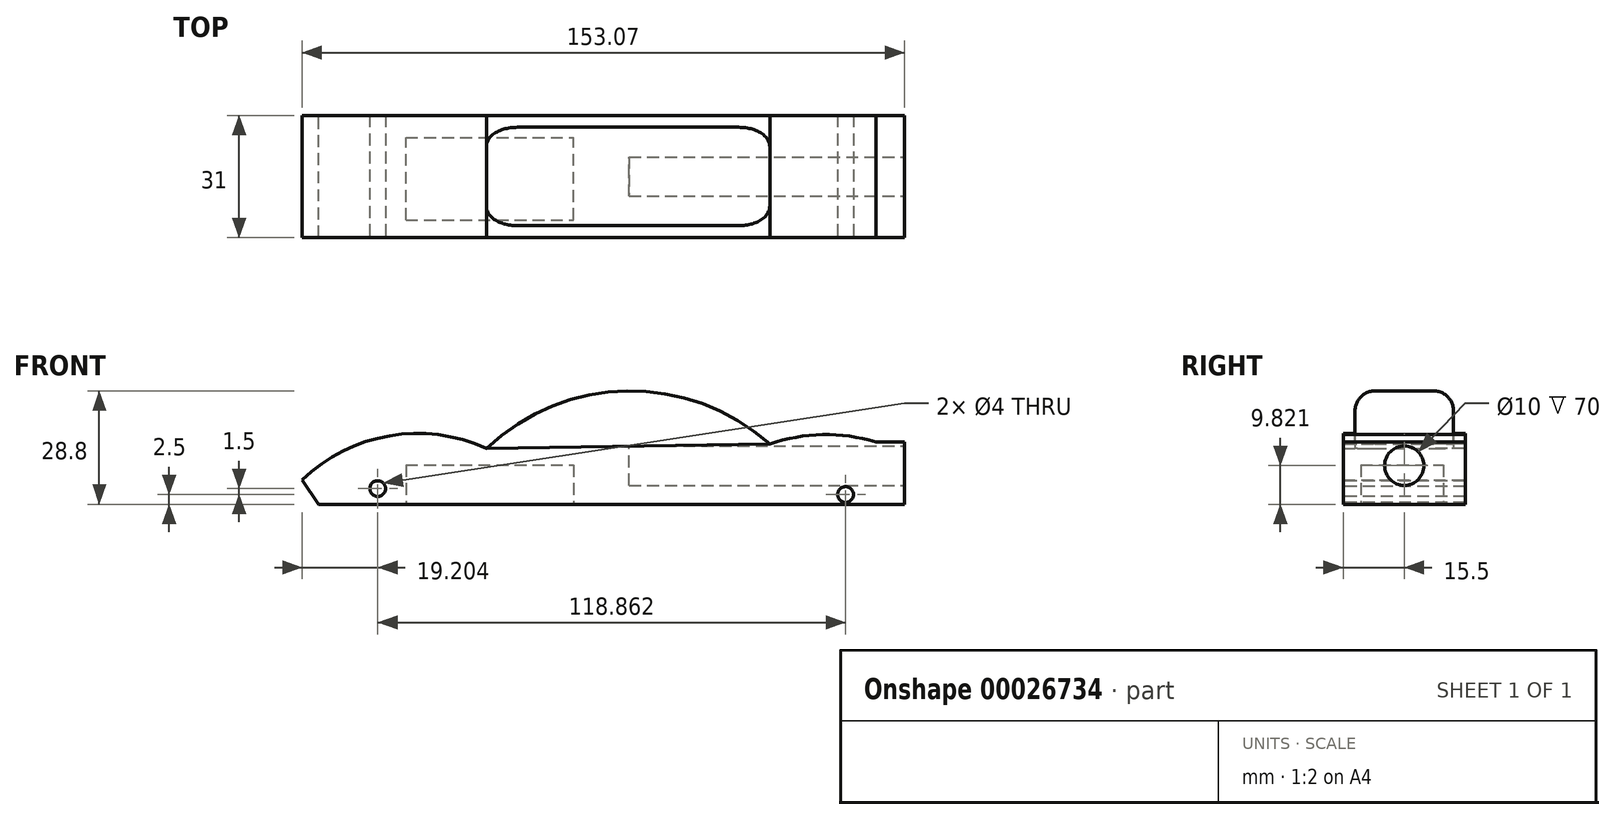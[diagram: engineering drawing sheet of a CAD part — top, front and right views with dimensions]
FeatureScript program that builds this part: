
annotation { "Feature Type Name" : "Feature", "Feature Type Description" : "" }
export const myFeature = defineFeature(function(context is Context, id is Id, definition is map)
    precondition{}
    {
        {
            var Q0;
            Q0=qCreatedBy(makeId("Front.planeOp"),FACE);
            var sketch = newSketch(context, id + "F0", { "sketchPlane" : qUnion([Q0])});
            skArc(sketch, "E0", {"start": v(-76.78, 0) * mm, "mid": v(-2.35, -2.55) * mm, "end": v(72.09, 0) * mm});
            skArc(sketch, "E1", {"start": v(-25.88, 9.16) * mm, "mid": v(2.62, 6.69) * mm, "end": v(30.71, 12.06) * mm});
            skArc(sketch, "E2", {"start": v(64.75, 15.82) * mm, "mid": v(47.34, 17.46) * mm, "end": v(30.71, 12.06) * mm});
            skLineSegment(sketch, "E3", {"start": v(-76.78, 0) * mm, "end": v(-80.98, 6.2) * mm});
            skArc(sketch, "E4", {"start": v(-25.88, 9.16) * mm, "mid": v(-53.98, 17.97) * mm, "end": v(-80.98, 6.2) * mm});
            skLineSegment(sketch, "E5", {"start": v(64.75, 15.82) * mm, "end": v(72.09, 15.82) * mm});
            skLineSegment(sketch, "E6", {"start": v(72.09, 15.82) * mm, "end": v(72.09, 0) * mm});
            skArc(sketch, "E7", {"start": v(37.83, 15.3) * mm, "mid": v(1.6, 28.8) * mm, "end": v(-34.18, 14.2) * mm});
            skSolve(sketch);
        }
        {
            var Q0;
            {var subQ3=sQuery(id+"F0.wireOp",EDGE,"E0");Q0=makeQuery(id+"F0.imprint","IMPRINT",FACE,{"disambiguationData":[TD([[makeQuery(id+"F0.imprint","IMPRINT",EDGE,{"derivedFrom":subQ3}),1.0]])]});}
            var Q1;
            {var subQ2=sQuery(id+"F0.wireOp",EDGE,"E1");Q1=makeQuery(id+"F0.imprint","IMPRINT",FACE,{"disambiguationData":[TD([[makeQuery(id+"F0.imprint","IMPRINT",EDGE,{"derivedFrom":subQ2}),1.0]])]});}
            extrude(context, id + "F1", {"entities" : qUnion([Q0, Q1]), "depth" : 25 * mm});
        }
        {
            var Q0;
            Q0=makeQuery(id+"F1.opExtrude","SWEPT_FACE",FACE,{"disambiguationData":[OSD([sQuery(id+"F0.wireOp",EDGE,"E6")])]});
            var sketch = newSketch(context, id + "F2", { "sketchPlane" : qUnion([Q0])});
            skCircle(sketch, "E8", {"center": v(-12.5, 9.82) * mm, "radius": 5 * mm});
            skSolve(sketch);
        }
        {
            var Q0;
            Q0=makeQuery(id+"F2.imprint","IMPRINT",FACE,{"disambiguationData":[TD([[makeQuery(id+"F2.imprint","IMPRINT",EDGE,{"derivedFrom":sQuery(id+"F2.wireOp",EDGE,"E8")}),1.0]])]});
            extrude(context, id + "F3", {"entities" : qUnion([Q0]), "operationType" : NewBodyOperationType.REMOVE, "oppositeDirection" : true, "depth" : 70 * mm});
        }
        {
            var Q0;
            Q0=makeQuery(id+"F3.boolean.opBoolean","COPY",FACE,{"derivedFrom":makeQuery(id+"F3.opExtrude","CAP_FACE",FACE,{"disambiguationData":[OSD([sQuery(id+"F2.wireOp",EDGE,"E8")])],"isStart":false})});
            var sketch = newSketch(context, id + "F4", { "sketchPlane" : qUnion([Q0])});
            skCircle(sketch, "E9", {"center": v(-12.5, 9.82) * mm, "radius": 5 * mm});
            skSolve(sketch);
        }
        {
            var Q0;
            Q0=sQuery(id+"F4.wireOp",EDGE,"E9");
            extrude(context, id + "F5", {"bodyType" : ToolBodyType.SURFACE, "surfaceEntities" : qUnion([Q0]), "depth" : 3 * mm});
        }
        {
            var Q0;
            Q0=makeQuery(id+"F1.opExtrude","CAP_FACE",FACE,{"disambiguationData":[OSD([sQuery(id+"F0.wireOp",EDGE,"E0"),sQuery(id+"F0.wireOp",EDGE,"E2"),sQuery(id+"F0.wireOp",EDGE,"E3"),sQuery(id+"F0.wireOp",EDGE,"E4"),sQuery(id+"F0.wireOp",EDGE,"E5"),sQuery(id+"F0.wireOp",EDGE,"E6"),sQuery(id+"F0.wireOp",EDGE,"E7")])],"isStart":false});
            var sketch = newSketch(context, id + "F6", { "sketchPlane" : qUnion([Q0])});
            skLineSegment(sketch, "E10", {"start": v(37.83, 15.3) * mm, "end": v(-34.18, 14.2) * mm});
            skSolve(sketch);
        }
        {
            var Q0;
            Q0=makeQuery(id+"F6.imprint","IMPRINT",FACE,{"disambiguationData":[TD([[makeQuery(id+"F6.imprint","IMPRINT",EDGE,{"derivedFrom":sQuery(id+"F6.wireOp",EDGE,"E10")}),1.0]])]});
            extrude(context, id + "F7", {"entities" : qUnion([Q0]), "operationType" : NewBodyOperationType.ADD, "depth" : 3 * mm});
        }
        {
            var Q0;
            Q0=makeQuery(id+"F1.opExtrude","CAP_FACE",FACE,{"disambiguationData":[OSD([sQuery(id+"F0.wireOp",EDGE,"E0"),sQuery(id+"F0.wireOp",EDGE,"E2"),sQuery(id+"F0.wireOp",EDGE,"E3"),sQuery(id+"F0.wireOp",EDGE,"E4"),sQuery(id+"F0.wireOp",EDGE,"E5"),sQuery(id+"F0.wireOp",EDGE,"E6"),sQuery(id+"F0.wireOp",EDGE,"E7")])],"isStart":true});
            var sketch = newSketch(context, id + "F8", { "sketchPlane" : qUnion([Q0])});
            skLineSegment(sketch, "E11", {"start": v(-37.83, 15.3) * mm, "end": v(34.18, 14.2) * mm});
            skSolve(sketch);
        }
        {
            var Q0;
            Q0 = qSketchRegion(id + "F8", true);
            var Q1;
            Q1=makeQuery(id+"F8.imprint","IMPRINT",FACE,{"disambiguationData":[TD([[makeQuery(id+"F8.imprint","IMPRINT",EDGE,{"derivedFrom":sQuery(id+"F8.wireOp",EDGE,"E11")}),-1.0]])]});
            extrude(context, id + "F9", {"entities" : qUnion([Q0, Q1]), "operationType" : NewBodyOperationType.ADD, "depth" : 3 * mm});
        }
        {
            var Q0;
            Q0=makeQuery(id+"F1.opExtrude","CAP_EDGE",EDGE,{"disambiguationData":[OSD([sQuery(id+"F0.wireOp",EDGE,"E7")])],"isStart":false});
            var Q1;
            Q1=makeQuery(id+"F1.opExtrude","CAP_EDGE",EDGE,{"disambiguationData":[OSD([sQuery(id+"F0.wireOp",EDGE,"E7")])],"isStart":true});
            fillet(context, id + "F10", {"entities" : qUnion([Q0, Q1]), "radius" : 5 * mm, "tangentPropagation" : true, "allowEdgeOverflow" : false});
        }
        {
            var Q0;
            Q0=makeQuery(id+"F7.opExtrude","CAP_FACE",FACE,{"disambiguationData":[OSD([sQuery(id+"F0.wireOp",EDGE,"E0"),sQuery(id+"F0.wireOp",EDGE,"E2"),sQuery(id+"F0.wireOp",EDGE,"E3"),sQuery(id+"F0.wireOp",EDGE,"E4"),sQuery(id+"F0.wireOp",EDGE,"E5"),sQuery(id+"F0.wireOp",EDGE,"E6"),sQuery(id+"F6.wireOp",EDGE,"E10")])],"isStart":false});
            var sketch = newSketch(context, id + "F11", { "sketchPlane" : qUnion([Q0])});
            skLineSegment(sketch, "E12", {"start": v(-76.78, 0) * mm, "end": v(72.09, 0) * mm});
            skSolve(sketch);
        }
        {
            var Q0;
            Q0=makeQuery(id+"F11.imprint","IMPRINT",FACE,{"disambiguationData":[TD([[makeQuery(id+"F11.imprint","IMPRINT",EDGE,{"derivedFrom":sQuery(id+"F11.wireOp",EDGE,"E12")}),-1.0]])]});
            extrude(context, id + "F12", {"entities" : qUnion([Q0]), "operationType" : NewBodyOperationType.REMOVE, "endBound" : BoundingType.THROUGH_ALL, "oppositeDirection" : true, "depth" : 25 * mm});
        }
        {
            var Q0;
            Q0=makeQuery(id+"F7.opExtrude","CAP_FACE",FACE,{"disambiguationData":[OSD([sQuery(id+"F0.wireOp",EDGE,"E0"),sQuery(id+"F0.wireOp",EDGE,"E2"),sQuery(id+"F0.wireOp",EDGE,"E3"),sQuery(id+"F0.wireOp",EDGE,"E4"),sQuery(id+"F0.wireOp",EDGE,"E5"),sQuery(id+"F0.wireOp",EDGE,"E6"),sQuery(id+"F6.wireOp",EDGE,"E10")])],"isStart":false});
            var sketch = newSketch(context, id + "F13", { "sketchPlane" : qUnion([Q0])});
            skLineSegment(sketch, "E13", {"start": v(-76.78, 0) * mm, "end": v(-61.78, 0) * mm});
            skLineSegment(sketch, "E14", {"start": v(72.09, 0) * mm, "end": v(57.09, 0) * mm});
            skLineSegment(sketch, "E15", {"start": v(57.09, 0) * mm, "end": v(57.09, 2.5) * mm});
            skCircle(sketch, "E16", {"center": v(57.09, 2.5) * mm, "radius": 2 * mm});
            skLineSegment(sketch, "E17", {"start": v(-61.78, 0) * mm, "end": v(-61.78, 4) * mm});
            skCircle(sketch, "E18", {"center": v(-61.78, 4) * mm, "radius": 2 * mm});
            skSolve(sketch);
        }
        {
            var Q0;
            Q0=makeQuery(id+"F13.imprint","IMPRINT",FACE,{"disambiguationData":[TD([[makeQuery(id+"F13.imprint","IMPRINT",EDGE,{"derivedFrom":sQuery(id+"F13.wireOp",EDGE,"E16")}),1.0]])]});
            var Q1;
            Q1=makeQuery(id+"F13.imprint","IMPRINT",FACE,{"disambiguationData":[TD([[makeQuery(id+"F13.imprint","IMPRINT",EDGE,{"derivedFrom":sQuery(id+"F13.wireOp",EDGE,"e984c35b-77bf-466f-8408-1bf98c32b081")}),1.0]])]});
            var Q2;
            Q2=makeQuery(id+"F13.imprint","IMPRINT",FACE,{"disambiguationData":[TD([[makeQuery(id+"F13.imprint","IMPRINT",EDGE,{"derivedFrom":sQuery(id+"F13.wireOp",EDGE,"E18")}),1.0]])]});
            extrude(context, id + "F14", {"entities" : qUnion([Q0, Q1, Q2]), "operationType" : NewBodyOperationType.REMOVE, "endBound" : BoundingType.THROUGH_ALL, "oppositeDirection" : true, "depth" : 25 * mm});
        }
        {
            var Q0;
            Q0=makeQuery(id+"F12.boolean.opBoolean","COPY",FACE,{"derivedFrom":makeQuery(id+"F12.opExtrude","SWEPT_FACE",FACE,{"disambiguationData":[OSD([sQuery(id+"F11.wireOp",EDGE,"E12")])]})});
            var sketch = newSketch(context, id + "F15", { "sketchPlane" : qUnion([Q0])});
            skLineSegment(sketch, "E19.bottom", {"start": v(-54.6, 23.55) * mm, "end": v(-12, 23.55) * mm});
            skLineSegment(sketch, "E19.top", {"start": v(-54.6, 2.6) * mm, "end": v(-12, 2.6) * mm});
            skLineSegment(sketch, "E19.left", {"start": v(-54.6, 23.55) * mm, "end": v(-54.6, 2.6) * mm});
            skLineSegment(sketch, "E19.right", {"start": v(-12, 23.55) * mm, "end": v(-12, 2.6) * mm});
            skSolve(sketch);
        }
        {
            var Q0;
            Q0=makeQuery(id+"F15.imprint","IMPRINT",FACE,{"disambiguationData":[TD([[makeQuery(id+"F15.imprint","IMPRINT",EDGE,{"derivedFrom":sQuery(id+"F15.wireOp",EDGE,"E19.bottom")}),-1.0]])]});
            extrude(context, id + "F16", {"entities" : qUnion([Q0]), "operationType" : NewBodyOperationType.REMOVE, "oppositeDirection" : true, "depth" : 10 * mm});
        }
    });
